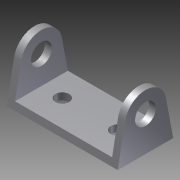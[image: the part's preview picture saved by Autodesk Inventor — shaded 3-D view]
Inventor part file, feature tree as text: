
AUTODESK INVENTOR PART (.ipt)
format: ipt  version: 2012 (Build 160160000, 160)  size: 121,856 bytes
history: native  units: in
note: dims shown in document units (in); Inventor stores cm internally (conversion verified against a paired STEP export)
features: extrude x3, sketch x3
ambient origin geometry x8: Origin, YZ Plane, XZ Plane, XY Plane, X Axis, Y Axis, Z Axis, Center Point
bodies: Solid1 (feature_tree)
feature tree (6):
  extrude  "Extrusion1"  Depth=2.0in
  extrude  "Extrusion2"  Depth=0.125in
  extrude  "Extrusion3"  Depth=1.0in TaperAngle=0.0deg
  sketch  "Sketch1"  dims[d0=1.0in d1=2.0in]
  sketch  "Sketch2"  dims[d2=0.125in d3=0.125in]
  sketch  "Sketch3"  dims[d4=0.125in d5=1.0in d6=0.0in d7=0.375in d8=0.625in d9=0.5in d10=1.0in d11=0.0in d12=0.25in d13=0.25in d14=0.5in d15=0.5in d16=0.5in d17=1.0in d18=0.0in]
